# Revit family: yara_single_-_yas_15000_vtl_r_sr_cee_00_c_114268000-00808703_e7ca
name_source: partatom
category: Lighting Fixtures
units: mm (PartAtom-declared; Revit-internal decimal feet)

## family parameters
Cut with Voids When Loaded = No
Host = Face
Light Source = No
Part Type = Normal
Room Calculation Point = No
Round Connector Dimension = Use Diameter
Shared = No

## types (1)
- YARA.single - YAS 15000/VTL/R/SR/CEE/00/C (1 x LED, 15000 lm, VTL)
    Apparent Load = 107 VA
    Approval mark = CE
    CIE Flux Codes = 58 87 97 13 100
    Color Rendering = 80-89
    Color Temperature = VTL
    Control Gear = Electronic ballast
    Default Elevation = 1800 mm
    Description = YAS 15000/VTL/R/SR/CEE/00/C|Free-standing luminaire|light source: LED Daylight 2700-6500 K  Energy efficiency category A/A+/A++|work equipment: Electronic ballast DALI|connected load: 220-240 V, 50/60 Hz|Power consumption: approx. 107 W|power factor: approx. 0,966|luminous flux: 15000 lm|luminous efficacy: 140 lm/W|light distribution: Direct/indirect|direct ratio: approx. 13 %|color rendering index (CRI): >= 80|chromaticity tolerance:  3 SDCM|technology: Presence and daylight sensor control (PIR)|operation: Wireless switch|luminaire body|material: Aluminium/plastic|surface: Powder coatet|colour: Silver metallic|lamp cover: Acrylic (PMMA), Satine, Structured|tubular section|material: Steel tube|surface: Powder-coated|Form: Tubular section upright|colour of tubular section: Silver metallic|luminaire base|Form: C-form flat|weight (net): approx. 18.0 kg|mains lead: 3.00 m Mains plug CEE 7/VII|Fastening: Floor standing base|glare control: Conical prismatic screen|luminance(L65): <= 2700 cd/m|unified glare rating(4H 8H): <=  16|special features: App control, Asymmetric radiation, Biodynamic light VTL, Direct and indirect lighting component with edge light and light guidetechnology for a homogeneous light exit, Flicker-free, Magnetic control panel, freely positionable, PIR movement and daylight sensor|Approval mark: VDE - ENEC|
    Frequency = 50 Hz, 60 Hz
    Height = 24 mm  [stored 0.0787402 ft]
    Lamp = 1 x LED
    Lamp Light Flux = 15000 lm
    Lamp count = 1
    Length = 690 mm
    Luminous efficacy = 140 lm/W
    Manufacturer = Waldmann
    ModVariant = No
    Model = 114268000-00808703
    Mounting Place = Floor
    Mounting Type = Freestanding
    Number of Poles = 1
    OnlyDefault = Yes
    Power Factor = 1
    Product Name = YARA.single - YAS 15000/VTL/R/SR/CEE/00/C
    Product group = Free standing luminaire
    ProductGroupID = 13
    Protection Class = Protection class I
    Protection Degree = IP 20
    RLX_Detail_Level = 1
    RlxData = <blob elided: 47117 chars, md5=64814f51>
    Socket = socket
    Standby Power = 0 W
    System Light Flux = 15000 lm
    System Power = 107 W
    Type Comments = Product without accessories
    Type Image = yas-r-sr-c.jpg
    URL = http://relux.com
    VarID = ---
    Voltage = 230 V
    Voltage Range = 220-240 V
    Weight = 0.00 kg
    Width = 358 mm

note: [stored X ft] marks values corroborated as IEEE doubles in the binary element streams (Revit-internal decimal feet)

## geometry (parser evidence)
native form markers: Sweep x14
no freeform markers — native parametric forms only
